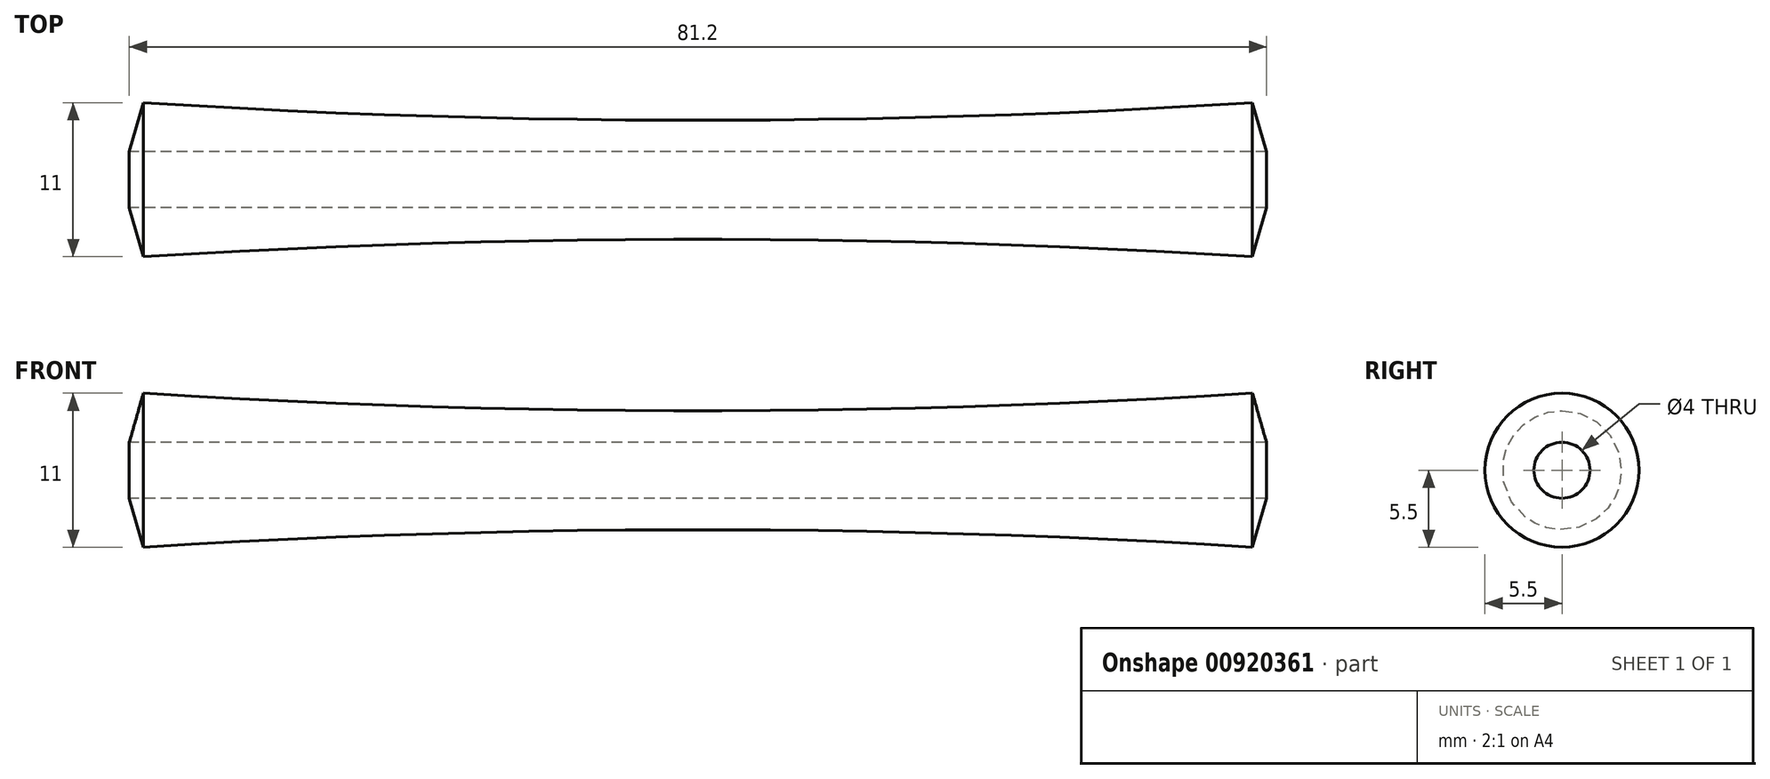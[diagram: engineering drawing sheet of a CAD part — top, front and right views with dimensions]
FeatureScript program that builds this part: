
annotation { "Feature Type Name" : "Feature", "Feature Type Description" : "" }
export const myFeature = defineFeature(function(context is Context, id is Id, definition is map)
    precondition{}
    {
        {
            var Q0;
            Q0=qCreatedBy(makeId("Front.planeOp"),FACE);
            var sketch = newSketch(context, id + "F0", { "sketchPlane" : qUnion([Q0])});
            skPoint(sketch, "E0", {"position": v(0, 4.25) * mm});
            skLineSegment(sketch, "E1", {"start": v(-40.6, 2) * mm, "end": v(40.6, 2) * mm});
            skPoint(sketch, "E2", {"position": v(-39.6, 5.5) * mm});
            skPoint(sketch, "E3.MirrorP", {"position": v(39.6, 5.5) * mm});
            skArc(sketch, "E4", {"start": v(-39.6, 5.5) * mm, "mid": v(0, 4.25) * mm, "end": v(39.6, 5.5) * mm});
            skLineSegment(sketch, "E5", {"start": v(-39.6, 5.5) * mm, "end": v(-40.6, 2) * mm});
            skLineSegment(sketch, "E6", {"start": v(39.6, 5.5) * mm, "end": v(40.6, 2) * mm});
            skLineSegment(sketch, "E7", {"start": v(-75.28, 0) * mm, "end": v(74.1, 0) * mm});
            skSolve(sketch);
        }
        {
            var Q0;
            Q0=makeQuery(id+"F0.imprint","IMPRINT",FACE,{"disambiguationData":[TD([[makeQuery(id+"F0.imprint","IMPRINT",EDGE,{"derivedFrom":sQuery(id+"F0.wireOp",EDGE,"E1")}),1.0]])]});
            var Q1;
            Q1=sQuery(id+"F0.wireOp",EDGE,"E7");
            revolve(context, id + "F1", {"surfaceOperationType" : NewSurfaceOperationType.NEW, "entities" : qUnion([Q0]), "axis" : qUnion([Q1]), "revolveType" : RevolveType.FULL});
        }
    });
